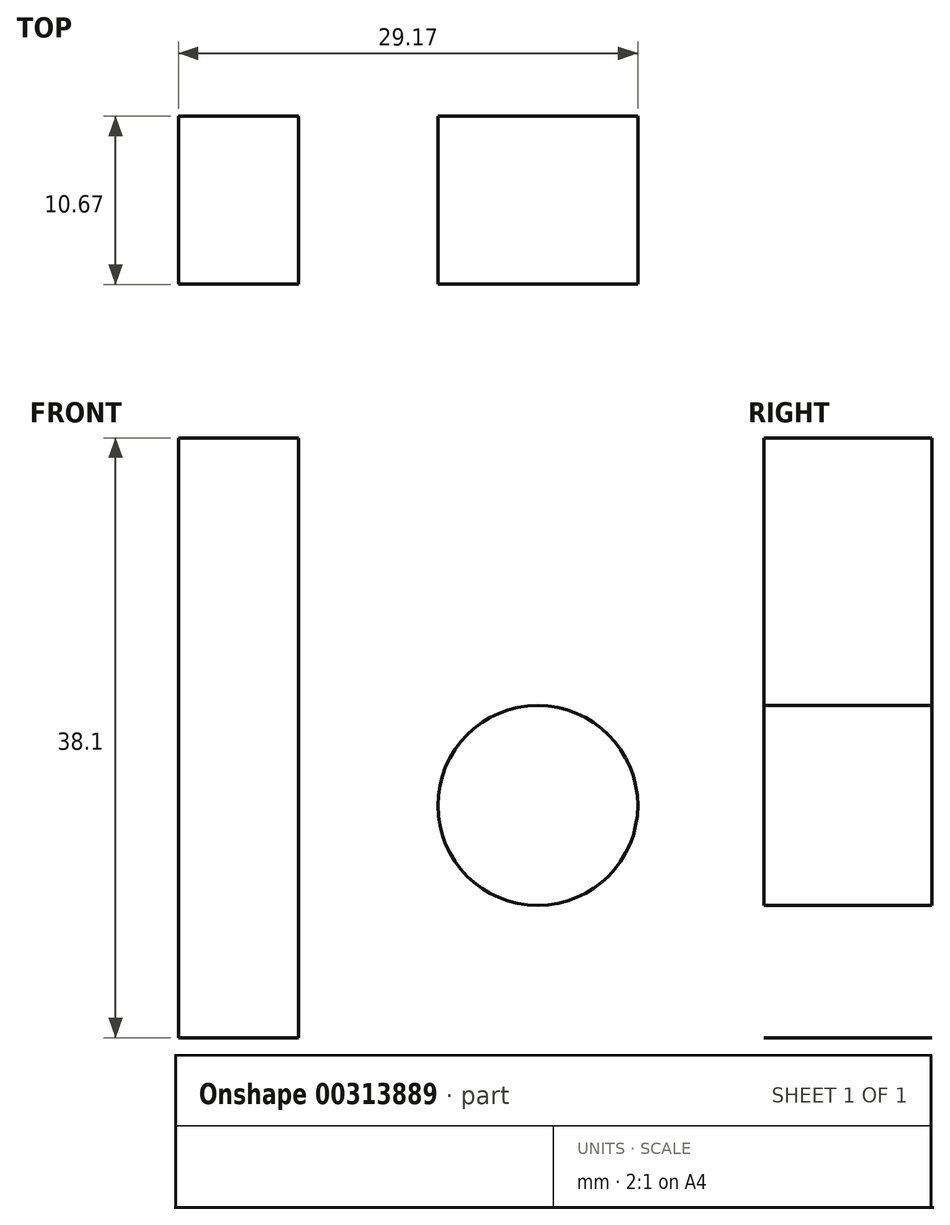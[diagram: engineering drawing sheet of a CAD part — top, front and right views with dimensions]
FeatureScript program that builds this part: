
annotation { "Feature Type Name" : "Feature", "Feature Type Description" : "" }
export const myFeature = defineFeature(function(context is Context, id is Id, definition is map)
    precondition{}
    {
        {
            var Q0;
            Q0=qCreatedBy(makeId("Front.planeOp"),FACE);
            var sketch = newSketch(context, id + "F0", { "sketchPlane" : qUnion([Q0])});
            skLineSegment(sketch, "E0.bottom", {"start": v(-7.62, 38.1) * mm, "end": v(0, 38.1) * mm});
            skLineSegment(sketch, "E0.top", {"start": v(-7.62, 0) * mm, "end": v(0, 0) * mm});
            skLineSegment(sketch, "E0.left", {"start": v(-7.62, 38.1) * mm, "end": v(-7.62, 0) * mm});
            skLineSegment(sketch, "E0.right", {"start": v(0, 38.1) * mm, "end": v(0, 0) * mm});
            skCircle(sketch, "E1", {"center": v(15.2, 14.75) * mm, "radius": 6.35 * mm});
            skSolve(sketch);
        }
        {
            var Q0;
            Q0 = qSketchRegion(id + "F0", true);
            extrude(context, id + "F1", {"entities" : qUnion([Q0]), "depth" : 10.67 * mm});
        }
    });
